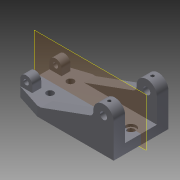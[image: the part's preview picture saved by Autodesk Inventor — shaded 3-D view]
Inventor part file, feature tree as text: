
AUTODESK INVENTOR PART (.ipt)
format: ipt  version: 2011 (Build 150229000, 229)  size: 183,296 bytes
history: native  units: mm
features: sketch x6, hole x5, extrude x3, plane x3, mirror x2, chamfer x2, fillet x1
ambient origin geometry x8: Origin, YZ Plane, XZ Plane, XY Plane, X Axis, Y Axis, Z Axis, Center Point
feature tree (22):
  extrude  "Extrusion1"  Depth=86.0mm
  extrude  "Extrusion2"  Depth=16.0mm
  fillet  "Fillet1"  Radius=53.0mm
  hole  "Hole1"  [1 undecoded]
  plane  "Work Plane1"
  mirror  "Mirror1"
  plane  "Work Plane2"
  extrude  "Extrusion3"  Depth=10.0mm
  hole  "Hole2"  [1 undecoded]
  mirror  "Mirror2"
  chamfer  "Chamfer1"  Distance=9.5mm
  chamfer  "Chamfer2"  Distance=25.0mm
  plane  "Work Plane3"
  hole  "Hole3"  [1 undecoded]
  hole  "Hole4"  [1 undecoded]
  hole  "Hole5"  [1 undecoded]
  sketch  "Sketch1"  dims[d0=160.0mm d1=86.0mm]
  sketch  "Sketch2"  dims[d2=15.0mm d3=0.0mm d4=16.0mm d5=53.0mm]
  sketch  "Sketch3"  dims[d6=3.490659mm d7=8.0mm]
  sketch  "Sketch4"  dims[d8=18.0mm d9=0.0mm d10=10.0mm d11=10.0mm]
  sketch  "Sketch5"  dims[d12=11.0mm d13=6.0mm d14=4.0mm d15=2.0mm d16=90.0deg d17=8.0mm d18=20.594885mm d19=8.0mm]
  sketch  "Sketch6"  dims[d20=30.0mm d21=9.5mm d22=25.0mm d23=14.0mm d24=0.0mm d25=10.0mm d26=10.0mm d27=8.0mm d28=6.0mm d29=4.0mm d30=2.0mm d31=90.0deg d32=8.0mm d33=20.594885mm d34=13.0mm d35=40.0mm d36=45.0deg d37=13.0mm d38=40.0mm d39=45.0deg d40=4.917mm d41=6.0mm d42=4.0mm d43=2.0mm d44=90.0deg d45=8.0mm d46=20.594885mm d47=16.0mm d48=32.0mm d49=33.0mm d50=11.0mm d51=6.0mm d52=4.0mm d53=2.0mm d54=90.0deg d55=8.0mm d56=20.594885mm d57=16.0mm d58=11.0mm d59=6.0mm d60=16.0mm d61=4.0mm d62=90.0deg d63=8.0mm d64=20.594885mm]
note: 5 required parameter values undecoded (feature->parameter linkage not recoverable at this tier; creation-order binding heuristic only, values carry confidence <= 0.55)
